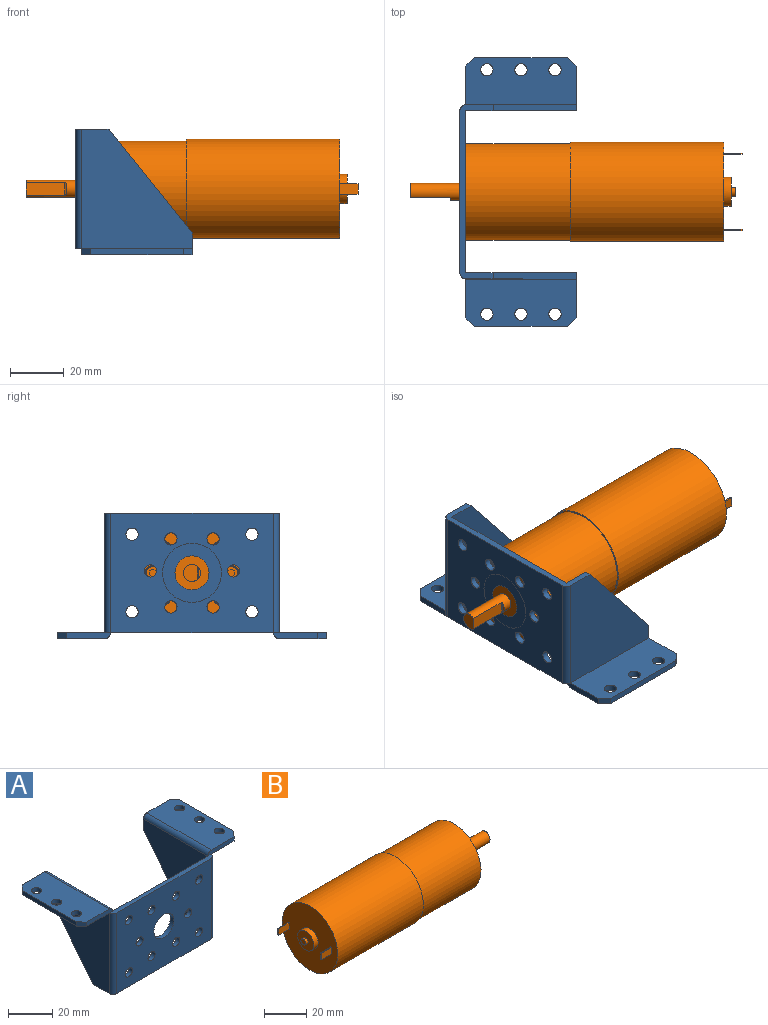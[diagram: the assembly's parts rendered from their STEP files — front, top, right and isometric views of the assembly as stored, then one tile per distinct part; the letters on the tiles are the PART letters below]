
ASSEMBLY  parts=2 mates=1
PART A: 47 faces, bbox 100.3x43.4x46.7 mm
  f0: plane 41.15x17.64mm, normal (0,0,1), area 666.2mm2, adj f4,f5,f6,f33,f34,f35,f36,f44
  f1: plane 41.15x17.64mm, normal (0,0,-1), area 666.2mm2, adj f3,f4,f5,f33,f34,f35,f36,f44
  f2: cylinder r=2.29mm len=4.57mm, axis (0,0,1), area 32.8mm2, adj f39,f40
  f3: plane 44.45x41.15mm, normal (-1,0,0), area 1230.4mm2, adj f1,f5,f15,f30,f32
  f4: plane 16.75x2.29mm, normal (0,-1,0), area 37mm2, adj f0,f1,f6,f7,f33
  f5: plane 16.76x8.1mm, normal (0,1,0), area 50.3mm2, adj f0,f1,f3,f6,f7,f14,f15,f36
  f6: cylinder r=2.54mm len=41.15mm, axis (0,1,0), area 143.8mm2, adj f0,f4,f5,f7
  f7: plane 65.02x43.43mm, normal (0,0,1), area 146.9mm2, adj f4,f5,f6,f9,f10,f11,f13,f14
  f8: plane 44.45x41.15mm, normal (1,0,0), area 1230.4mm2, adj f9,f11,f12,f32,f40
  f9: cylinder r=2.54mm len=44.45mm, axis (0,0,1), area 155.3mm2, adj f7,f8,f28,f32
  f10: plane 16.75x2.29mm, normal (0,-1,0), area 37mm2, adj f7,f39,f40,f43,f46
  f11: plane 16.76x8.1mm, normal (0,1,0), area 50.3mm2, adj f7,f8,f12,f13,f39,f40,f41,f46
  f12: plane 38.64x30.99mm, normal (0,0.78,-0.63), area 113.2mm2, adj f8,f11,f13,f32
  f13: plane 44.45x41.15mm, normal (-1,0,0), area 1230.4mm2, adj f7,f11,f12,f31,f32
  f14: plane 44.45x41.15mm, normal (1,0,0), area 1230.4mm2, adj f5,f7,f15,f31,f32
  f15: plane 38.64x30.99mm, normal (0,0.78,-0.63), area 113.2mm2, adj f3,f5,f14,f32
  f16: cylinder r=6.35mm len=12.7mm, axis (0,1,0), area 91.2mm2, adj f27,f31
  f17: cylinder r=2.29mm len=4.57mm, axis (0,1,0), area 32.8mm2, adj f27,f31
  f18: cylinder r=2.29mm len=4.57mm, axis (0,1,0), area 32.8mm2, adj f27,f31
  f19: cylinder r=2.29mm len=4.57mm, axis (0,1,0), area 32.8mm2, adj f27,f31
  f20: cylinder r=2.29mm len=4.57mm, axis (0,1,0), area 32.8mm2, adj f27,f31
  f21: cylinder r=2.29mm len=4.57mm, axis (0,1,0), area 32.8mm2, adj f27,f31
  f22: cylinder r=2.29mm len=4.57mm, axis (0,1,0), area 32.8mm2, adj f27,f31
  f23: cylinder r=2.29mm len=4.57mm, axis (0,1,0), area 32.8mm2, adj f27,f31
  f24: cylinder r=2.29mm len=4.57mm, axis (0,1,0), area 32.8mm2, adj f27,f31
  f25: cylinder r=2.29mm len=4.57mm, axis (0,1,0), area 32.8mm2, adj f27,f31
  f26: cylinder r=2.29mm len=4.57mm, axis (0,1,0), area 32.8mm2, adj f27,f31
  f27: plane 60.45x44.45mm, normal (0,-1,0), area 2396.2mm2, adj f7,f16,f17,f18,f19,f20,f21,f22
  f28: plane 44.45x0.01mm, normal (1,0,0), area 0.5mm2, adj f7,f9,f27,f32
  f29: plane 44.45x0.01mm, normal (-1,0,0), area 0.5mm2, adj f7,f27,f30,f32
  f30: cylinder r=2.54mm len=44.45mm, axis (0,0,-1), area 155.3mm2, adj f3,f7,f29,f32
  f31: plane 60.45x44.45mm, normal (0,1,0), area 2396.2mm2, adj f7,f13,f14,f16,f17,f18,f19,f20
  f32: plane 65.02x12.45mm, normal (0,0,-1), area 192.4mm2, adj f3,f8,f9,f12,f13,f14,f15,f27
  f33: plane 3.3x3.16mm, normal (-0.72,-0.69,0), area 10.5mm2, adj f0,f1,f4,f35
  f34: cylinder r=2.29mm len=4.57mm, axis (0,0,1), area 32.8mm2, adj f0,f1
  f35: plane 34.54x2.29mm, normal (-1,0,0), area 79mm2, adj f0,f1,f33,f36
  f36: plane 3.3x3.16mm, normal (-0.72,0.69,0), area 10.5mm2, adj f0,f1,f5,f35
  f37: cylinder r=2.29mm len=4.57mm, axis (0,0,1), area 32.8mm2, adj f39,f40
  f38: cylinder r=2.29mm len=4.57mm, axis (0,0,1), area 32.8mm2, adj f39,f40
  f39: plane 41.15x17.64mm, normal (0,0,1), area 666.2mm2, adj f2,f10,f11,f37,f38,f41,f42,f43
  f40: plane 41.15x17.64mm, normal (0,0,-1), area 666.2mm2, adj f2,f8,f10,f11,f37,f38,f41,f42
  f41: plane 3.3x3.16mm, normal (0.72,0.69,0), area 10.5mm2, adj f11,f39,f40,f42
  f42: plane 34.54x2.29mm, normal (1,0,0), area 79mm2, adj f39,f40,f41,f43
  f43: plane 3.3x3.16mm, normal (0.72,-0.69,0), area 10.5mm2, adj f10,f39,f40,f42
  f44: cylinder r=2.29mm len=4.57mm, axis (0,0,1), area 32.8mm2, adj f0,f1
  f45: cylinder r=2.29mm len=4.57mm, axis (0,0,1), area 32.8mm2, adj f0,f1
  f46: cylinder r=2.54mm len=41.15mm, axis (0,-1,0), area 143.8mm2, adj f7,f10,f11,f39
PART B: 82 faces, bbox 123.9x37x37 mm
  f0: torus R=2.41mm, axis (1,0,0), area 6.5mm2, adj f7,f49
  f1: torus R=2.41mm, axis (1,0,0), area 6.5mm2, adj f6,f50
  f2: torus R=2.41mm, axis (1,0,0), area 6.5mm2, adj f5,f51
  f3: torus R=2.41mm, axis (1,0,0), area 6.5mm2, adj f4,f52
  f4: cylinder r=2.67mm len=5.33mm, axis (-1,0,0), area 76.6mm2, adj f3,f22
  f5: cylinder r=2.67mm len=5.33mm, axis (-1,0,0), area 76.6mm2, adj f2,f23
  f6: cylinder r=2.67mm len=5.33mm, axis (-1,0,0), area 76.6mm2, adj f1,f24
  f7: cylinder r=2.67mm len=5.33mm, axis (-1,0,0), area 76.6mm2, adj f0,f25
  f8: cylinder r=2.82mm len=5.64mm, axis (1,0,0), area 90mm2, adj f22,f29
  f9: cylinder r=2.82mm len=5.64mm, axis (1,0,0), area 90mm2, adj f23,f29
  f10: cylinder r=2.82mm len=5.64mm, axis (1,0,0), area 90mm2, adj f24,f29
  f11: cylinder r=2.82mm len=5.64mm, axis (1,0,0), area 90mm2, adj f25,f29
  f12: cylinder r=1.59mm len=3.18mm, axis (1,0,0), area 16.1mm2, adj f27,f38
  f13: cylinder r=5.44mm len=10.87mm, axis (1,0,0), area 97.2mm2, adj f26,f27
  f14: cylinder r=1.73mm len=6mm, axis (1,0,0), area 65.1mm2, adj f29,f37
  f15: cylinder r=1.73mm len=6mm, axis (1,0,0), area 65.1mm2, adj f29,f36
  f16: cylinder r=1.73mm len=6mm, axis (1,0,0), area 65.1mm2, adj f29,f35
  f17: cylinder r=1.73mm len=6mm, axis (1,0,0), area 65.1mm2, adj f29,f34
  f18: cylinder r=3.16mm len=18.52mm, axis (-1,0,0), area 286.1mm2, adj f28,f31,f32,f33,f81
  f19: cylinder r=11mm len=22mm, axis (-1,0,0), area 159.8mm2, adj f28,f29
  f20: cylinder r=18mm len=39.01mm, axis (-1,0,0), area 4412.4mm2, adj f29,f30
  f21: cylinder r=18.5mm len=57.15mm, axis (1,0,0), area 6643.1mm2, adj f26,f30
  f22: plane 5.64x5.64mm, normal (1,0,0), area 2.6mm2, adj f4,f8
  f23: plane 5.64x5.64mm, normal (1,0,0), area 2.6mm2, adj f5,f9
  f24: plane 5.64x5.64mm, normal (1,0,0), area 2.6mm2, adj f6,f10
  f25: plane 5.64x5.64mm, normal (1,0,0), area 2.6mm2, adj f7,f11
  f26: plane 37x37mm, normal (-1,0,0), area 978.5mm2, adj f13,f21,f39,f40,f41,f42,f44,f45
  f27: plane 10.87x10.87mm, normal (-1,0,0), area 84.9mm2, adj f12,f13
  f28: plane 22x22mm, normal (1,0,0), area 348.7mm2, adj f18,f19
  f29: plane 36x36mm, normal (1,0,0), area 500.4mm2, adj f8,f9,f10,f11,f14,f15,f16,f17
  f30: plane 37x37mm, normal (1,0,0), area 57.3mm2, adj f20,f21
  f31: plane 3.73x0.61mm, normal (1,0,0), area 1.5mm2, adj f18,f81
  f32: plane 14.49x4.82mm, normal (0,1,0), area 69.9mm2, adj f18,f33,f81
  f33: plane 6.32x5.21mm, normal (1,0,0), area 27.7mm2, adj f18,f32
  f34: plane 3.45x3.45mm, normal (1,0,0), area 9.4mm2, adj f17
  f35: plane 3.45x3.45mm, normal (1,0,0), area 9.4mm2, adj f16
  f36: plane 3.45x3.45mm, normal (1,0,0), area 9.4mm2, adj f15
  f37: plane 3.45x3.45mm, normal (1,0,0), area 9.4mm2, adj f14
  f38: plane 3.18x3.18mm, normal (-1,0,0), area 7.9mm2, adj f12
  f39: plane 6.86x0.51mm, normal (0,0,1), area 3.5mm2, adj f26,f40,f42,f43
  f40: plane 6.86x3.86mm, normal (0,1,0), area 26.5mm2, adj f26,f39,f41,f43
  f41: plane 6.86x0.51mm, normal (0,0,-1), area 3.5mm2, adj f26,f40,f42,f43
  f42: plane 6.86x3.86mm, normal (0,-1,0), area 26.5mm2, adj f26,f39,f41,f43
  f43: plane 3.86x0.51mm, normal (-1,0,0), area 2mm2, adj f39,f40,f41,f42
  f44: plane 6.86x0.51mm, normal (0,0,1), area 3.5mm2, adj f26,f45,f47,f48
  f45: plane 6.86x3.86mm, normal (0,1,0), area 26.5mm2, adj f26,f44,f46,f48
  f46: plane 6.86x0.51mm, normal (0,0,-1), area 3.5mm2, adj f26,f45,f47,f48
  f47: plane 6.86x3.86mm, normal (0,-1,0), area 26.5mm2, adj f26,f44,f46,f48
  f48: plane 3.86x0.51mm, normal (-1,0,0), area 2mm2, adj f44,f45,f46,f47
  f49: plane 4.83x4.83mm, normal (1,0,0), area 12.7mm2, adj f0,f53,f54,f55,f56,f57,f58
  f50: plane 4.83x4.83mm, normal (1,0,0), area 12.7mm2, adj f1,f60,f61,f62,f63,f64,f65
  f51: plane 4.83x4.83mm, normal (1,0,0), area 12.7mm2, adj f2,f67,f68,f69,f70,f71,f72
  f52: plane 4.83x4.83mm, normal (1,0,0), area 12.7mm2, adj f3,f74,f75,f76,f77,f78,f79
  f53: plane 2.54x1.27mm, normal (0,0.5,0.87), area 3.7mm2, adj f49,f54,f58,f59
  f54: plane 2.54x1.47mm, normal (0,1,0), area 3.7mm2, adj f49,f53,f55,f59
  f55: plane 2.54x1.27mm, normal (0,0.5,-0.87), area 3.7mm2, adj f49,f54,f56,f59
  f56: plane 2.54x1.27mm, normal (0,-0.5,-0.87), area 3.7mm2, adj f49,f55,f57,f59
  f57: plane 2.54x1.47mm, normal (0,-1,0), area 3.7mm2, adj f49,f56,f58,f59
  f58: plane 2.54x1.27mm, normal (0,-0.5,0.87), area 3.7mm2, adj f49,f53,f57,f59
  f59: plane 2.93x2.54mm, normal (1,0,0), area 5.6mm2, adj f53,f54,f55,f56,f57,f58
  f60: plane 2.54x1.27mm, normal (0,0.5,0.87), area 3.7mm2, adj f50,f61,f65,f66
  f61: plane 2.54x1.47mm, normal (0,1,0), area 3.7mm2, adj f50,f60,f62,f66
  f62: plane 2.54x1.27mm, normal (0,0.5,-0.87), area 3.7mm2, adj f50,f61,f63,f66
  f63: plane 2.54x1.27mm, normal (0,-0.5,-0.87), area 3.7mm2, adj f50,f62,f64,f66
  f64: plane 2.54x1.47mm, normal (0,-1,0), area 3.7mm2, adj f50,f63,f65,f66
  f65: plane 2.54x1.27mm, normal (0,-0.5,0.87), area 3.7mm2, adj f50,f60,f64,f66
  f66: plane 2.93x2.54mm, normal (1,0,0), area 5.6mm2, adj f60,f61,f62,f63,f64,f65
  f67: plane 2.54x1.27mm, normal (0,0.49,0.87), area 3.7mm2, adj f51,f68,f72,f73
  f68: plane 2.54x1.47mm, normal (0,1,0.01), area 3.7mm2, adj f51,f67,f69,f73
  f69: plane 2.54x1.27mm, normal (0,0.51,-0.86), area 3.7mm2, adj f51,f68,f70,f73
  f70: plane 2.54x1.27mm, normal (0,-0.49,-0.87), area 3.7mm2, adj f51,f69,f71,f73
  f71: plane 2.54x1.47mm, normal (0,-1,-0.01), area 3.7mm2, adj f51,f70,f72,f73
  f72: plane 2.54x1.27mm, normal (0,-0.51,0.86), area 3.7mm2, adj f51,f67,f71,f73
  f73: plane 2.93x2.55mm, normal (1,0,0), area 5.6mm2, adj f67,f68,f69,f70,f71,f72
  f74: plane 2.54x1.27mm, normal (0,0.5,0.87), area 3.7mm2, adj f52,f75,f79,f80
  f75: plane 2.54x1.47mm, normal (0,1,0), area 3.7mm2, adj f52,f74,f76,f80
  f76: plane 2.54x1.27mm, normal (0,0.5,-0.87), area 3.7mm2, adj f52,f75,f77,f80
  f77: plane 2.54x1.27mm, normal (0,-0.5,-0.87), area 3.7mm2, adj f52,f76,f78,f80
  f78: plane 2.54x1.47mm, normal (0,-1,0), area 3.7mm2, adj f52,f77,f79,f80
  f79: plane 2.54x1.27mm, normal (0,-0.5,0.87), area 3.7mm2, adj f52,f74,f78,f80
  f80: plane 2.93x2.54mm, normal (1,0,0), area 5.6mm2, adj f74,f75,f76,f77,f78,f79
  f81: cylinder r=0.51mm len=4.82mm, axis (0,0,1), area 3.4mm2, adj f18,f31,f32
PLACE A rot(axis=(0.71,0.71,0),180deg) t=(0,-30.23,44.45)mm
PLACE B rot(axis=(0,0,1),180deg) t=(41.33,0,22.22)mm
MATE fastened B.f12 <-> A.f16  axis (-1,0,0) through (0,0,22.22)mm
